# Revit family: PRD_FrankeWS_JntrlUnits_SiriusMultiPurposeSink_BS311N,BS312N
name_source: partatom
category: Plumbing Fixtures
revit_build: Autodesk Revit 2018 (Build: 20190510_1515(x64)
units: mm (PartAtom-declared; Revit-internal decimal feet)

## family parameters
Cut with Voids When Loaded = No
Host = Face
OmniClass Number = 23.45.05.14.14
OmniClass Title = Sinks/Lavatories
Part Type = Normal
Room Calculation Point = No
Round Connector Dimension = Use Diameter
Shared = No

## types (2) — shared parameters
AssetType = Fixed
Category = Pr_40_20_96_44, Janitorial sinks
Color = Stainless steel
Default Elevation = 850 mm  [stored 2.78871 ft]
DrainSize = DN 40 (1 1/2 inch.)
DurationUnit = year
Features = stainless steel, 0.8 mm, satin finished, wall mounting, 700x328x460 mm (WxHxD)
Finish = Satin finished
FinishAndMaterial = Stainless steel 1.4301
Form = Stainless steel multi purpose sink
FrameMaterial = PRD_AR_StainlessSteel_SatinFinished
GrossWeight = 7.70 kg
IfcExportAs = IfcSanitaryTerminalType
IfcExportType = SINK
Manufacturer = KWC Group AG
ManufacturerName = KWC Group AG
ManufacturerURL = www.kwc.com
Material = Stainless steel
NBSDescription = Janitorial units
NBSReference = 45-35-70/401
NetWeight = 6.70 kg
NominalDepth = 460 mm  [stored 1.50919 ft]
NominalHeight = 328 mm  [stored 1.07612 ft]
NominalWidth = 700 mm  [stored 2.29659 ft]
OutletSize = DN 40 (1 1/2 inch.)
ProductInformation = https://pim.kwc.com
Shape = Rectangular
SinkMaterial = PRD_AR_StainlessSteel_SatinFinished
SinkMounting = WallHung
SinkType = Other
Size = 700 x 460 x 328 mm
URL = www.kwc.com
Uniclass2015Code = Pr_40_20_96_44
Uniclass2015Title = Janitorial sinks
Uniclass2015Version = Products v1.10
Version = 1
WarrantyDurationUnit = year
WasteSize = 40  [stored 0.131234 ft]
WaterSupplyOverflowAndWasteHolesOverflow = Stand pipe overflow
WaterSupplyOverflowAndWasteHolesWaterSupply = No tapholes

## per-type parameters (varying)
| type | BIMObjectName | Description | Left | ModelNumber | Name | Right | WaterSupplyOverflowAndWasteHolesWaste |
| BS311N | PRD_AR_JanitorialUnits_SiriusMultiPurposeSink_BS311N | SIRIUS washtrough for wall mounting, stainless steel, satin finished surface, material thickness of trough 0.8 mm / side panels 1.2 mm, side panels with integrated wall brackets, seamlessly welded, front panel with rubbing board, no tap ledge, no overflow, with grey plastic frame, 45 mm rear upstand, left hand waste, G 1 1/2 B plastic standpipe strainer, includes fixings. | Yes | 2030045749 | Sirius multi purpose sink BS311N | No | Left-Back-Corner |
| BS312N | PRD_AR_JanitorialUnits_SiriusMultiPurposeSink_BS312N | SIRIUS washtrough for wall mounting, stainless steel, satin finished surface, material thickness of trough 0.8 mm / side panels 1.2 mm, side panels with integrated wall brackets, seamlessly welded, front panel with rubbing board, no tap ledge, no overflow, with grey plastic frame, 45 mm rear upstand, right hand drain, G 1 1/2 B plastic standpipe strainer, includes fixings. | No | 2030045750 | Sirius multi purpose sink BS312N | Yes | Right-Back-Corner |

note: column(s) folded — value = type name in every type: Model, ModelReference

note: [stored X ft] marks values corroborated as IEEE doubles in the binary element streams (Revit-internal decimal feet)

## geometry (parser evidence)
native form markers: Sweep x4
no freeform markers — native parametric forms only
